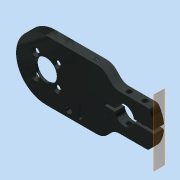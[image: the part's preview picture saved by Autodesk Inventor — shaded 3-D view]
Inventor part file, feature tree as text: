
AUTODESK INVENTOR PART (.ipt)
format: ipt  version: 2015 (Build 190159000, 159)  size: 200,704 bytes
history: native  units: in
note: dims shown in document units (in); Inventor stores cm internally (conversion verified against a paired STEP export)
features: other x3, plane x1
ambient origin geometry x8: Origin, YZ Plane, XZ Plane, XY Plane, X Axis, Y Axis, Z Axis, Center Point
bodies: Solid1 (feature_tree)
feature tree (4):
  other  "MotorMount.ipt"
  plane  "Work Plane1"
  other  "Solid2::MotorMount.ipt"
  other  "TaggingFeature1"
